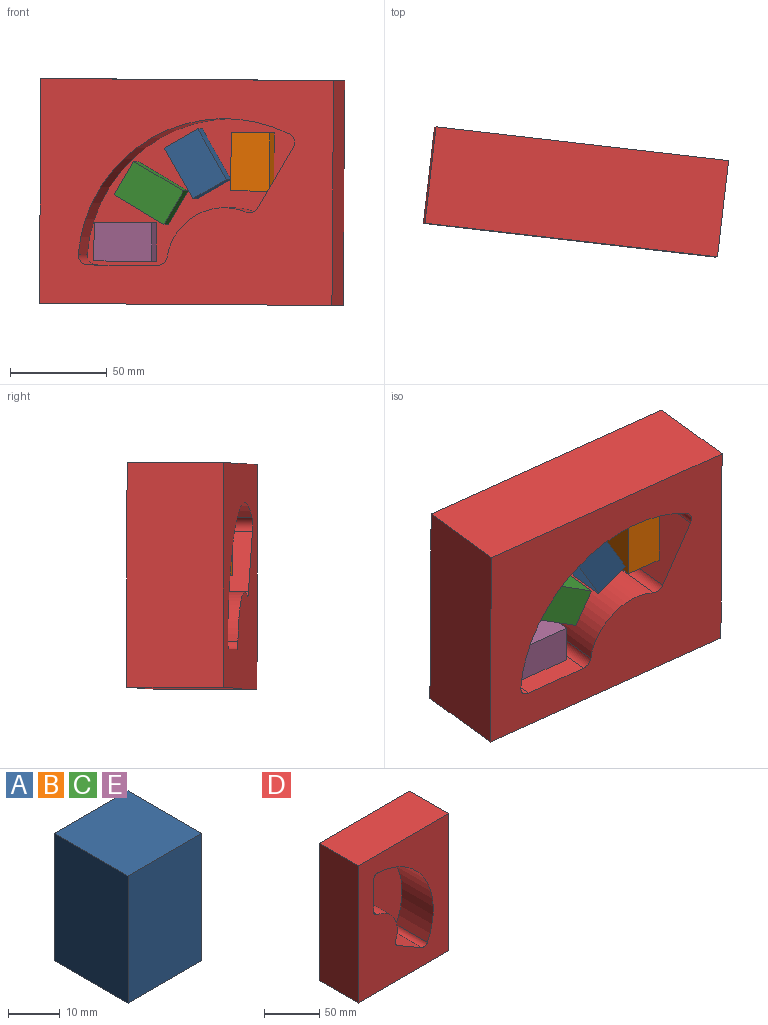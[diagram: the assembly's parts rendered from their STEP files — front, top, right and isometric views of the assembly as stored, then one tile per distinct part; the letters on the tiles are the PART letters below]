
ASSEMBLY  parts=5 mates=1
PART A: 6 faces, bbox 20x20x30 mm
  f0: plane 30x20mm, normal (1,0,0), area 600mm2, adj f1,f3,f4,f5
  f1: plane 20x20mm, normal (0,0,1), area 400mm2, adj f0,f2,f4,f5
  f2: plane 30x20mm, normal (-1,0,0), area 600mm2, adj f1,f3,f4,f5
  f3: plane 20x20mm, normal (0,0,-1), area 400mm2, adj f0,f2,f4,f5
  f4: plane 30x20mm, normal (0,-1,0), area 600mm2, adj f0,f1,f2,f3
  f5: plane 30x20mm, normal (0,1,0), area 600mm2, adj f0,f1,f2,f3
PART B: same geometry as A
PART C: same geometry as A
PART D: 15 faces, bbox 116x50x151.9 mm
  f0: plane 116x50mm, normal (0,0,1), area 5800mm2, adj f1,f11,f12,f13
  f1: plane 151.91x50mm, normal (-1,0,0), area 7595.3mm2, adj f0,f2,f12,f13
  f2: plane 116x50mm, normal (0,0,-1), area 5800mm2, adj f1,f11,f12,f13
  f3: cylinder r=5mm len=40mm, axis (0,1,0), area 328.3mm2, adj f4,f10,f12,f14
  f4: cylinder r=76mm len=109.08mm, axis (0,1,0), area 5938.4mm2, adj f3,f5,f12,f14
  f5: cylinder r=5mm len=40mm, axis (0,1,0), area 328.3mm2, adj f4,f6,f12,f14
  f6: plane 40x31.34mm, normal (0.5,0,0.87), area 1447.3mm2, adj f5,f7,f12,f14
  f7: cylinder r=5mm len=40mm, axis (0,1,0), area 285.5mm2, adj f6,f8,f12,f14
  f8: cylinder r=30mm len=40.83mm, axis (0,1,0), area 2169.2mm2, adj f7,f9,f12,f14
  f9: cylinder r=5mm len=40mm, axis (0,1,0), area 285.5mm2, adj f8,f10,f12,f14
  f10: plane 40x36.18mm, normal (1,0,0), area 1447.3mm2, adj f3,f9,f12,f14
  f11: plane 151.91x50mm, normal (1,0,0), area 7595.3mm2, adj f0,f2,f12,f13
  f12: plane 151.91x116mm, normal (0,-1,0), area 12535.4mm2, adj f0,f1,f2,f3,f4,f5,f6,f7
  f13: plane 151.91x116mm, normal (0,1,0), area 17621mm2, adj f0,f1,f2,f11
  f14: plane 111.91x76mm, normal (0,-1,0), area 5085.7mm2, adj f3,f4,f5,f6,f7,f8,f9,f10
PART E: same geometry as A
PLACE A rot(axis=(0.06,1,-0.02),150.5deg) t=(17.79,83.45,57.24)mm
PLACE B rot(axis=(-0.06,-1,0),179.6deg) t=(46.09,80.19,58.19)mm
PLACE C rot(axis=(0.06,1,-0.03),120.5deg) t=(-6.26,86.22,42.17)mm
PLACE D rot(axis=(-0.06,-1,-0.06),89.8deg) t=(36.1,102.46,4.53)mm
PLACE E rot(axis=(0.06,1,-0.06),90.6deg) t=(-19.6,87.75,17.02)mm
MATE slider D.f10 <-> E.f0  axis (0.01,0,1) through (-19.72,78.7,4.92)mm
